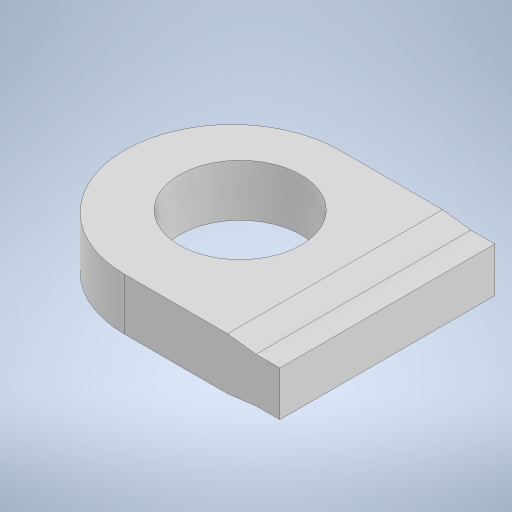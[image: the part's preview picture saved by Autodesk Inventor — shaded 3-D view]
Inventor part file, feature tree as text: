
AUTODESK INVENTOR PART (.ipt)
format: ipt  version: 2024 (Build 280153000, 153)  size: 241,664 bytes
history: native  units: in
note: dims shown in document units (in); Inventor stores cm internally (conversion verified against a paired STEP export)
features: extrude x3, sketch x3
ambient origin geometry x8: Origin, YZ Plane, XZ Plane, XY Plane, X Axis, Y Axis, Z Axis, Center Point
bodies: Solid1 (feature_tree)
feature tree (6):
  extrude  "Extrusion1"  Depth=3.6in
  extrude  "Extrusion2"  Depth=0.4in
  extrude  "Extrusion3"  Depth=0.75in
  sketch  "Sketch1"  dims[d0=4.4in d1=3.6in]
  sketch  "Sketch2"  dims[d2=0.87in d3=0.0in d4=0.4in]
  sketch  "Sketch3"  dims[d5=0.75in d6=0.475in d7=10.0in d8=0.0in d9=0.88in d10=0.68in d11=1.545in d12=10.0in d13=0.0in]
